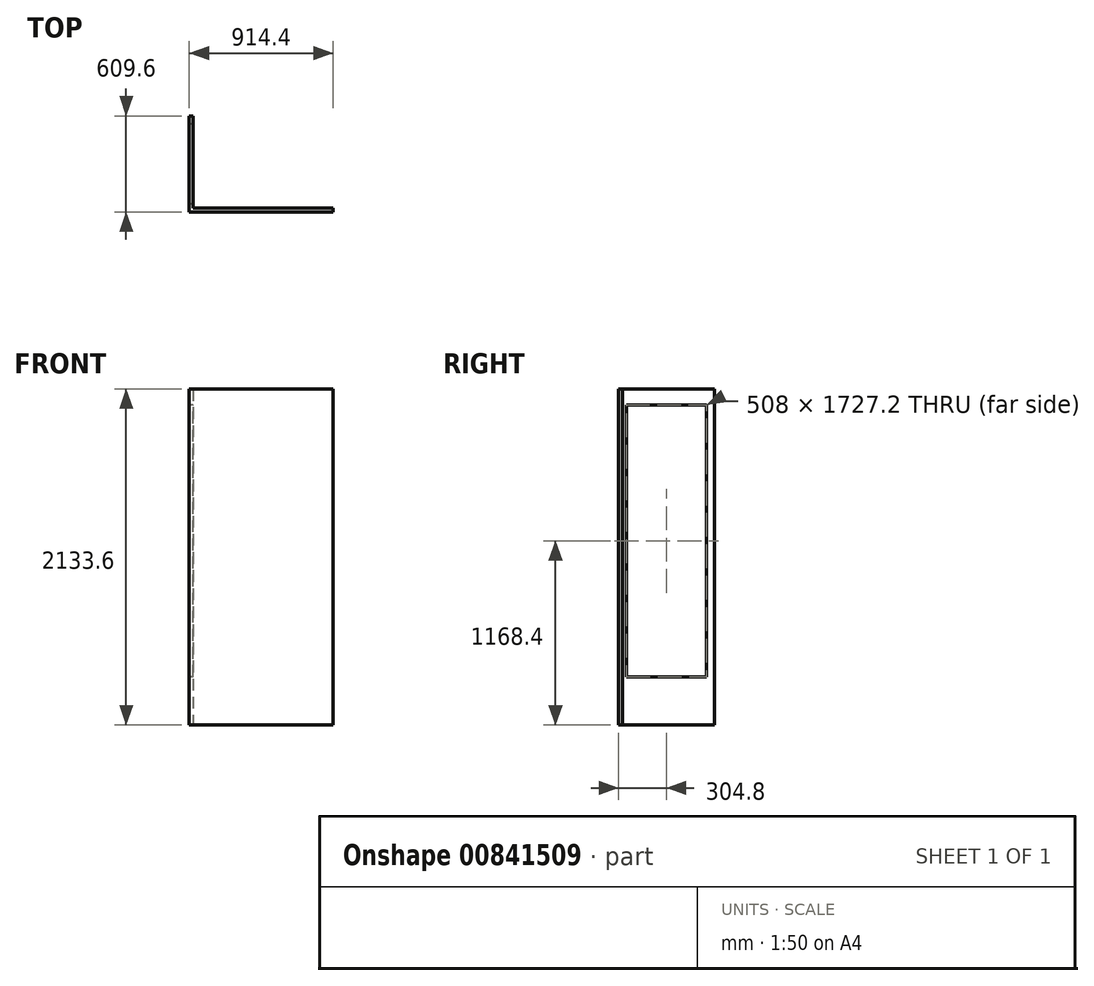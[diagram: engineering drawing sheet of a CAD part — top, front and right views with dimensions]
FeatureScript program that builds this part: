
annotation { "Feature Type Name" : "Feature", "Feature Type Description" : "" }
export const myFeature = defineFeature(function(context is Context, id is Id, definition is map)
    precondition{}
    {
        {
            var Q0;
            Q0=qCreatedBy(makeId("Top.planeOp"),FACE);
            var sketch = newSketch(context, id + "F0", { "sketchPlane" : qUnion([Q0])});
            skLineSegment(sketch, "E0", {"start": v(0, 0) * mm, "end": v(0, 609.6) * mm});
            skLineSegment(sketch, "E1", {"start": v(0, 609.6) * mm, "end": v(25.4, 609.6) * mm});
            skLineSegment(sketch, "E2", {"start": v(25.4, 609.6) * mm, "end": v(25.4, 25.4) * mm});
            skLineSegment(sketch, "E3", {"start": v(25.4, 25.4) * mm, "end": v(914.4, 25.4) * mm});
            skLineSegment(sketch, "E4", {"start": v(914.4, 25.4) * mm, "end": v(914.4, 0) * mm});
            skLineSegment(sketch, "E5", {"start": v(914.4, 0) * mm, "end": v(0, 0) * mm});
            skSolve(sketch);
        }
        {
            var Q0;
            Q0=qSketchRegion(id+"F0",true);
            extrude(context, id + "F1", {"entities" : qUnion([Q0]), "depth" : 2133.6 * mm, "offsetDistance" : 25.4 * mm});
        }
        {
            var Q0;
            Q0=makeQuery(id+"F1.opExtrude","SWEPT_FACE",FACE,{"disambiguationData":[OSD([sQuery(id+"F0.wireOp",EDGE,"E0")])]});
            var sketch = newSketch(context, id + "F2", { "sketchPlane" : qUnion([Q0])});
            skLineSegment(sketch, "E6.bottom", {"start": v(-558.8, 2032) * mm, "end": v(-50.8, 2032) * mm});
            skLineSegment(sketch, "E6.top", {"start": v(-558.8, 304.8) * mm, "end": v(-50.8, 304.8) * mm});
            skLineSegment(sketch, "E6.left", {"start": v(-558.8, 2032) * mm, "end": v(-558.8, 304.8) * mm});
            skLineSegment(sketch, "E6.right", {"start": v(-50.8, 2032) * mm, "end": v(-50.8, 304.8) * mm});
            skSolve(sketch);
        }
        {
            var Q0;
            Q0=qSketchRegion(id+"F2",true);
            extrude(context, id + "F3", {"entities" : qUnion([Q0]), "operationType" : NewBodyOperationType.REMOVE, "endBound" : BoundingType.THROUGH_ALL, "oppositeDirection" : true, "depth" : 25.4 * mm, "offsetDistance" : 25.4 * mm});
        }
    });
